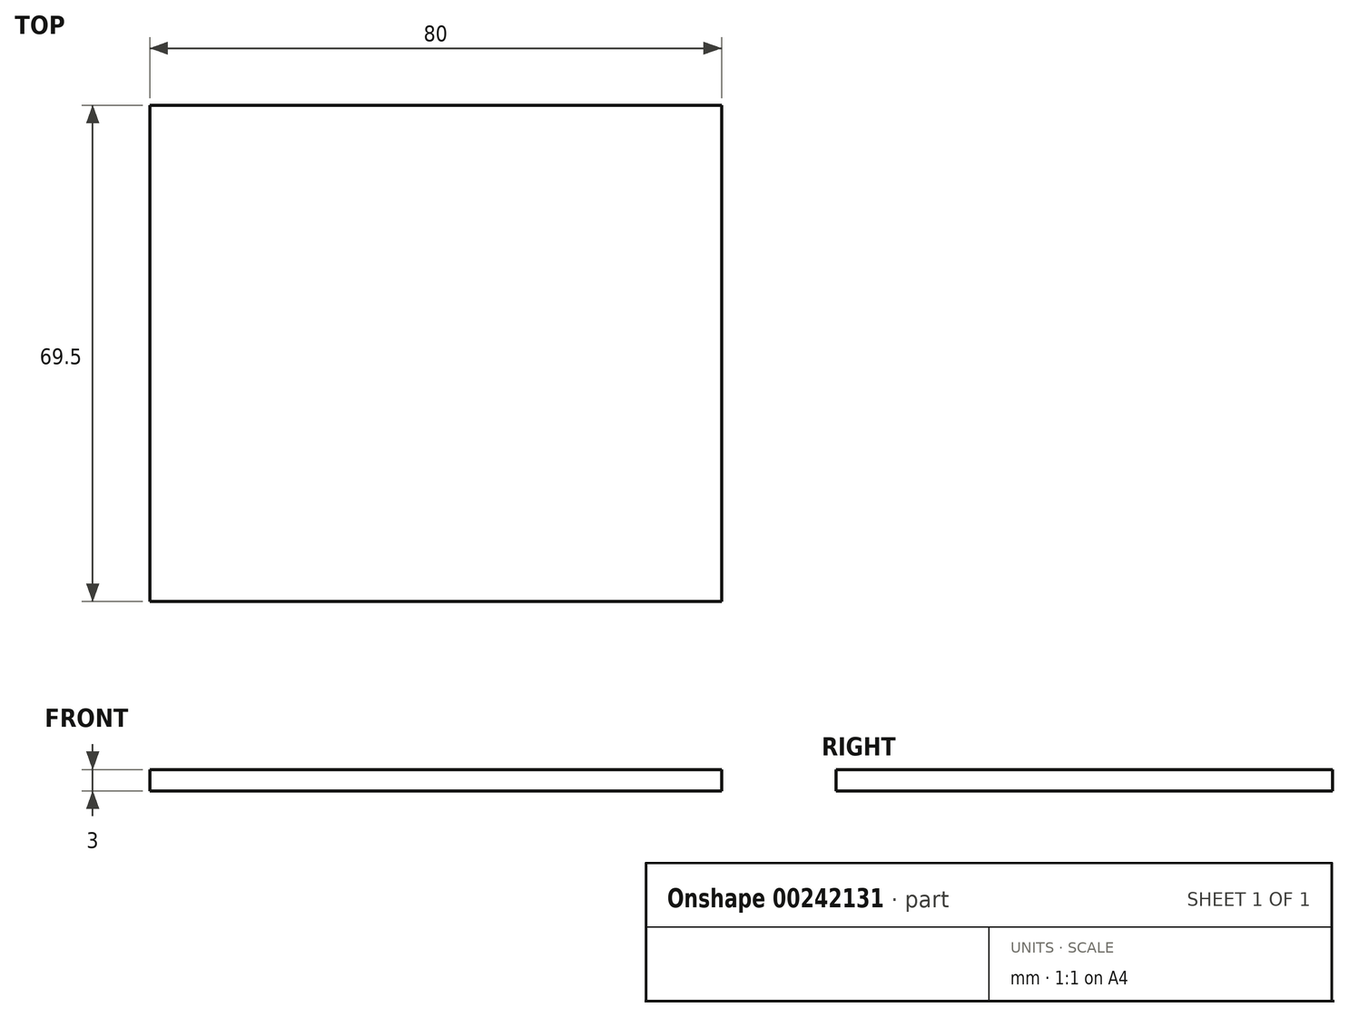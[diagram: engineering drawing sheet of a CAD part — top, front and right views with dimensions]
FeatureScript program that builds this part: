
annotation { "Feature Type Name" : "Feature", "Feature Type Description" : "" }
export const myFeature = defineFeature(function(context is Context, id is Id, definition is map)
    precondition{}
    {
        {
            var Q0;
            Q0=qCreatedBy(makeId("Top.planeOp"),FACE);
            var sketch = newSketch(context, id + "F0", { "sketchPlane" : qUnion([Q0])});
            skLineSegment(sketch, "E0.bottom", {"start": v(-40, 40) * mm, "end": v(40, 40) * mm});
            skLineSegment(sketch, "E0.top", {"start": v(-40, -40) * mm, "end": v(-20.27, -40) * mm});
            skLineSegment(sketch, "E0.left", {"start": v(-40, 40) * mm, "end": v(-40, -40) * mm});
            skLineSegment(sketch, "E0.right", {"start": v(40, 40) * mm, "end": v(40, -40) * mm});
            skPoint(sketch, "E0.middle", {"position": v(0, 0) * mm});
            skLineSegment(sketch, "E1", {"start": v(-20.27, -40) * mm, "end": v(-20.27, -29.5) * mm});
            skLineSegment(sketch, "E2", {"start": v(-20.27, -29.5) * mm, "end": v(-9.77, -29.5) * mm});
            skLineSegment(sketch, "E3", {"start": v(-9.77, -29.5) * mm, "end": v(-9.77, -40) * mm});
            skLineSegment(sketch, "E4", {"start": v(9.83, -40) * mm, "end": v(9.83, -29.5) * mm});
            skLineSegment(sketch, "E5", {"start": v(9.83, -29.5) * mm, "end": v(20.33, -29.5) * mm});
            skLineSegment(sketch, "E6", {"start": v(20.33, -29.5) * mm, "end": v(20.33, -40) * mm});
            skLineSegment(sketch, "E7.trimOffspring", {"start": v(-9.77, -40) * mm, "end": v(9.83, -40) * mm});
            skLineSegment(sketch, "E8.trimOffspring", {"start": v(20.33, -40) * mm, "end": v(40, -40) * mm});
            skLineSegment(sketch, "E9", {"start": v(-20.27, -29.5) * mm, "end": v(-40, -29.5) * mm});
            skLineSegment(sketch, "E10", {"start": v(-9.77, -29.5) * mm, "end": v(9.83, -29.5) * mm});
            skLineSegment(sketch, "E11", {"start": v(20.33, -29.5) * mm, "end": v(40, -29.5) * mm});
            skSolve(sketch);
        }
        {
            var Q0;
            {var subQ2=sQuery(id+"F0.wireOp",EDGE,"E0.bottom");Q0=makeQuery(id+"F0.imprint","IMPRINT",FACE,{"disambiguationData":[TD([[makeQuery(id+"F0.imprint","IMPRINT",EDGE,{"derivedFrom":subQ2}),-1.0]])]});}
            extrude(context, id + "F1", {"entities" : qUnion([Q0]), "depth" : 3 * mm});
        }
        {
            var Q0;
            Q0=makeQuery(id+"F1.opExtrude","CAP_FACE",FACE,{"disambiguationData":[OSD([sQuery(id+"F0.wireOp",EDGE,"E0.bottom"),sQuery(id+"F0.wireOp",EDGE,"E0.left"),sQuery(id+"F0.wireOp",EDGE,"E0.right"),sQuery(id+"F0.wireOp",EDGE,"E2"),sQuery(id+"F0.wireOp",EDGE,"E5"),sQuery(id+"F0.wireOp",EDGE,"E9"),sQuery(id+"F0.wireOp",EDGE,"E10"),sQuery(id+"F0.wireOp",EDGE,"E11")])],"isStart":false});
            cPlane(context, id + "F2", {"entities" : qUnion([Q0]), "cplaneType" : CPlaneType.OFFSET, "offset" : 50 * mm, "width" : 150 * mm, "height" : 150 * mm});
        }
    });
